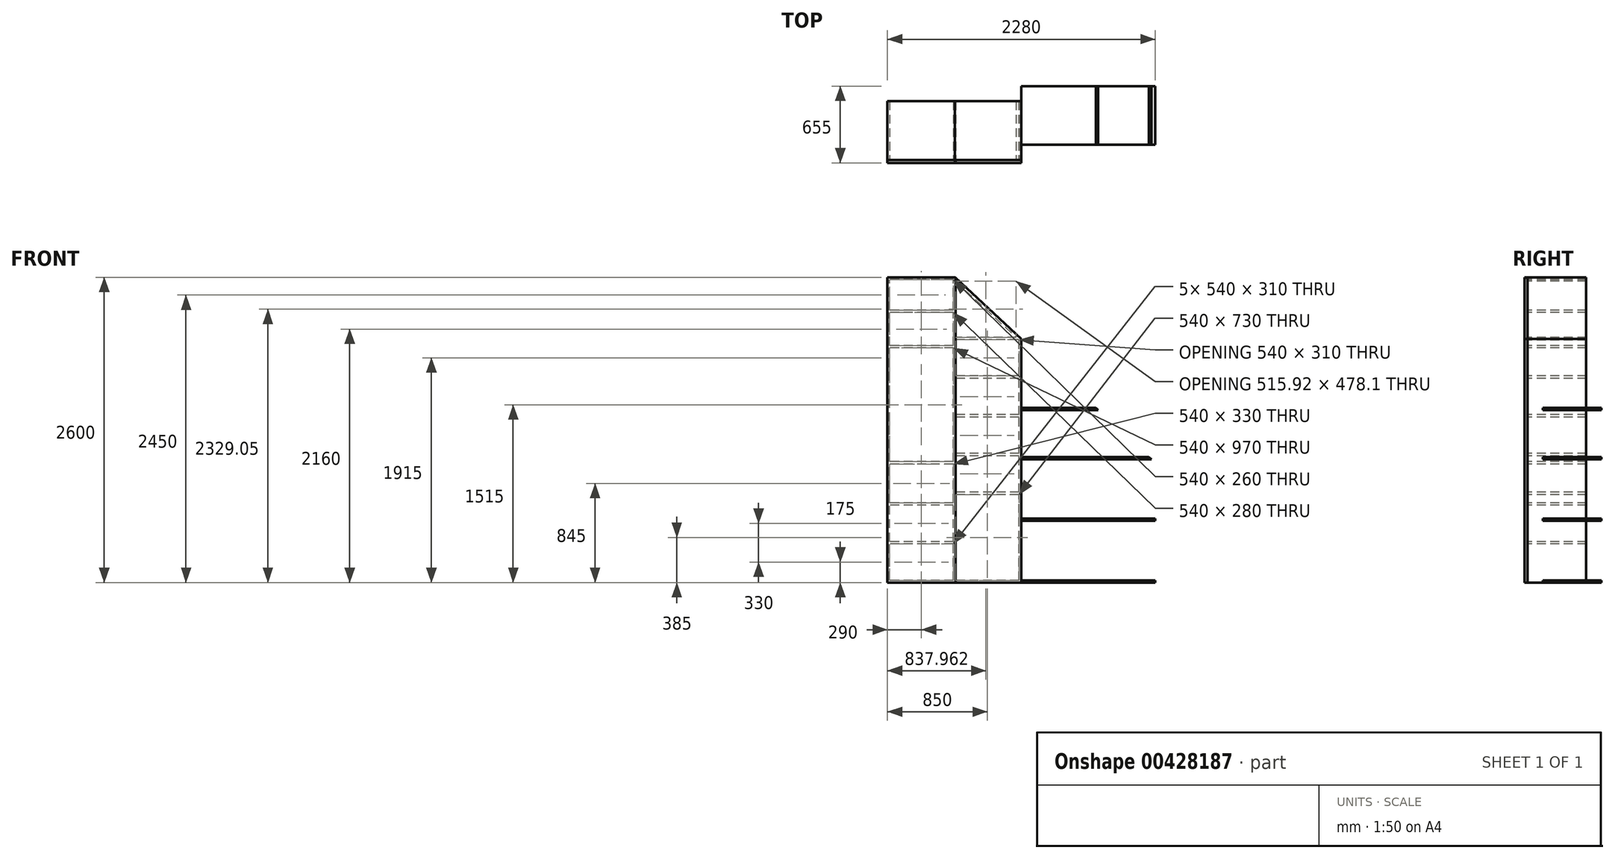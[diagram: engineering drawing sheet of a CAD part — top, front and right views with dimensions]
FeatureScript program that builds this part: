
annotation { "Feature Type Name" : "Feature", "Feature Type Description" : "" }
export const myFeature = defineFeature(function(context is Context, id is Id, definition is map)
    precondition{}
    {
        {
            var Q0;
            Q0=qCreatedBy(makeId("Front.planeOp"),FACE);
            var sketch = newSketch(context, id + "F0", { "sketchPlane" : qUnion([Q0])});
            skLineSegment(sketch, "E0.bottom", {"start": v(1140, -1300) * mm, "end": v(-1140, -1300) * mm});
            skLineSegment(sketch, "E0.top", {"start": v(-565, 1300) * mm, "end": v(-1140, 1300) * mm});
            skLineSegment(sketch, "E0.left", {"start": v(1140, -1300) * mm, "end": v(1140, -280) * mm});
            skLineSegment(sketch, "E0.right", {"start": v(-1140, -1300) * mm, "end": v(-1140, 1300) * mm});
            skPoint(sketch, "E0.middle", {"position": v(0, 0) * mm});
            skLineSegment(sketch, "E1", {"start": v(-565, 1300) * mm, "end": v(1140, -280) * mm});
            skLineSegment(sketch, "E2.0", {"start": v(-20, -1280) * mm, "end": v(-20, -550) * mm});
            skLineSegment(sketch, "E3.0", {"start": v(-580, -1280) * mm, "end": v(-580, -970) * mm});
            skLineSegment(sketch, "E4.0", {"start": v(-20, -1050) * mm, "end": v(-560, -1050) * mm});
            skLineSegment(sketch, "E5.0", {"start": v(-20, -800) * mm, "end": v(-560, -800) * mm});
            skLineSegment(sketch, "E6.0", {"start": v(-20, -550) * mm, "end": v(-560, -550) * mm});
            skLineSegment(sketch, "E7.0", {"start": v(-580, -325) * mm, "end": v(-1120, -325) * mm});
            skLineSegment(sketch, "E8.trimOffspring", {"start": v(-580, 700) * mm, "end": v(-1120, 700) * mm});
            skLineSegment(sketch, "E9.0", {"start": v(-580, 1000) * mm, "end": v(-1120, 1000) * mm});
            skLineSegment(sketch, "E10.0", {"start": v(-580, -640) * mm, "end": v(-1120, -640) * mm});
            skLineSegment(sketch, "E11.trimOffspring", {"start": v(-580, -970) * mm, "end": v(-1120, -970) * mm});
            skLineSegment(sketch, "E12.0", {"start": v(-580, 670) * mm, "end": v(-1120, 670) * mm});
            skLineSegment(sketch, "E13.0", {"start": v(-580, 650) * mm, "end": v(-1120, 650) * mm});
            skLineSegment(sketch, "E14.0", {"start": v(-580, -270) * mm, "end": v(-1120, -270) * mm});
            skLineSegment(sketch, "E15.0", {"start": v(-580, -345) * mm, "end": v(-1120, -345) * mm});
            skLineSegment(sketch, "E16.0", {"start": v(1140, -775) * mm, "end": v(0, -775) * mm});
            skLineSegment(sketch, "E17", {"start": v(1140, -280) * mm, "end": v(0, -280) * mm, "construction": true});
            skLineSegment(sketch, "E18.0", {"start": v(1107.63, -250) * mm, "end": v(-20, -250) * mm});
            skLineSegment(sketch, "E19.0", {"start": v(654.4, 170) * mm, "end": v(0, 170) * mm});
            skLineSegment(sketch, "E20.0", {"start": v(-1120, -1280) * mm, "end": v(-1120, -970) * mm});
            skLineSegment(sketch, "E21.0", {"start": v(-560, -1300) * mm, "end": v(-560, 1268.1) * mm});
            skLineSegment(sketch, "E22.0", {"start": v(0, -1300) * mm, "end": v(0, 776.42) * mm});
            skLineSegment(sketch, "E23.0", {"start": v(-580, 1280) * mm, "end": v(-1120, 1280) * mm});
            skLineSegment(sketch, "E24.0", {"start": v(-560, 1268.1) * mm, "end": v(-44.08, 790) * mm});
            skLineSegment(sketch, "E25.0", {"start": v(1140, -755) * mm, "end": v(0, -755) * mm});
            skLineSegment(sketch, "E26.0", {"start": v(-580, 1020) * mm, "end": v(-1120, 1020) * mm});
            skLineSegment(sketch, "E27.0", {"start": v(-580, 720) * mm, "end": v(-1120, 720) * mm});
            skLineSegment(sketch, "E28.0", {"start": v(-580, -290) * mm, "end": v(-1120, -290) * mm});
            skLineSegment(sketch, "E29.0", {"start": v(-580, -620) * mm, "end": v(-1120, -620) * mm});
            skLineSegment(sketch, "E30.0", {"start": v(-580, -950) * mm, "end": v(-1120, -950) * mm});
            skLineSegment(sketch, "E31.0", {"start": v(1140, -1280) * mm, "end": v(0, -1280) * mm});
            skLineSegment(sketch, "E32.trimOffspring", {"start": v(1086.04, -230) * mm, "end": v(0, -230) * mm});
            skLineSegment(sketch, "E33.trimOffspring", {"start": v(632.82, 190) * mm, "end": v(0, 190) * mm});
            skLineSegment(sketch, "E34.trimOffspring", {"start": v(-1120, 1020) * mm, "end": v(-1120, 1280) * mm});
            skLineSegment(sketch, "E35.trimOffspring", {"start": v(-1120, 720) * mm, "end": v(-1120, 1000) * mm});
            skLineSegment(sketch, "E36.trimOffspring", {"start": v(-580, 720) * mm, "end": v(-580, 1000) * mm});
            skLineSegment(sketch, "E37.trimOffspring", {"start": v(-580, 1020) * mm, "end": v(-580, 1280) * mm});
            skLineSegment(sketch, "E38.trimOffspring", {"start": v(-1120, -270) * mm, "end": v(-1120, 700) * mm});
            skLineSegment(sketch, "E39.trimOffspring", {"start": v(-580, -270) * mm, "end": v(-580, 700) * mm});
            skLineSegment(sketch, "E40.trimOffspring", {"start": v(-20, 375) * mm, "end": v(-20, 440) * mm});
            skLineSegment(sketch, "E41.trimOffspring", {"start": v(-20, 720) * mm, "end": v(-20, 767.69) * mm});
            skPoint(sketch, "E42.orphan", {"position": v(-20, -280) * mm});
            skLineSegment(sketch, "E43.trimOffspring", {"start": v(-20, -285) * mm, "end": v(-20, -220) * mm});
            skPoint(sketch, "E44.orphan", {"position": v(-580, -550) * mm});
            skPoint(sketch, "E45.orphan", {"position": v(-580, -800) * mm});
            skLineSegment(sketch, "E46.trimOffspring", {"start": v(-580, -950) * mm, "end": v(-580, -640) * mm});
            skLineSegment(sketch, "E47.trimOffspring", {"start": v(-580, -620) * mm, "end": v(-580, -290) * mm});
            skLineSegment(sketch, "E48.trimOffspring", {"start": v(-580, -1280) * mm, "end": v(-1120, -1280) * mm});
            skPoint(sketch, "E49.orphan", {"position": v(-1140, -970) * mm});
            skLineSegment(sketch, "E50.trimOffspring", {"start": v(-1120, -950) * mm, "end": v(-1120, -640) * mm});
            skPoint(sketch, "E51.orphan", {"position": v(-1140, -640) * mm});
            skLineSegment(sketch, "E52.trimOffspring", {"start": v(-1120, -620) * mm, "end": v(-1120, -290) * mm});
            skLineSegment(sketch, "E53.trimOffspring", {"start": v(-20, -1280) * mm, "end": v(-560, -1280) * mm});
            skLineSegment(sketch, "E54", {"start": v(-560, 1268.1) * mm, "end": v(-560, 1295.37) * mm});
            skLineSegment(sketch, "E55.0", {"start": v(-20, -220) * mm, "end": v(-560, -220) * mm});
            skLineSegment(sketch, "E56.0", {"start": v(-20, 110) * mm, "end": v(-560, 110) * mm});
            skLineSegment(sketch, "E57.0", {"start": v(-20, 440) * mm, "end": v(-560, 440) * mm});
            skLineSegment(sketch, "E58.0", {"start": v(-20, 770) * mm, "end": v(-560, 770) * mm});
            skLineSegment(sketch, "E59.0", {"start": v(-44.08, 790) * mm, "end": v(-560, 790) * mm});
            skLineSegment(sketch, "E60.0", {"start": v(-20, 460) * mm, "end": v(-560, 460) * mm});
            skLineSegment(sketch, "E61.0", {"start": v(-20, 130) * mm, "end": v(-560, 130) * mm});
            skLineSegment(sketch, "E62.0", {"start": v(-20, -200) * mm, "end": v(-560, -200) * mm});
            skLineSegment(sketch, "E63.0", {"start": v(-20, -530) * mm, "end": v(-560, -530) * mm});
            skLineSegment(sketch, "E64.trimOffspring", {"start": v(-22.5, 770) * mm, "end": v(-20, 767.69) * mm});
            skLineSegment(sketch, "E65.trimOffspring", {"start": v(-20, 460) * mm, "end": v(-20, 700) * mm});
            skLineSegment(sketch, "E66.trimOffspring", {"start": v(-20, 130) * mm, "end": v(-20, 355) * mm});
            skLineSegment(sketch, "E67.trimOffspring", {"start": v(-20, -200) * mm, "end": v(-20, 110) * mm});
            skLineSegment(sketch, "E68.trimOffspring", {"start": v(-20, -530) * mm, "end": v(-20, -305) * mm});
            skLineSegment(sketch, "E69", {"start": v(-20, 720) * mm, "end": v(-20, 700) * mm});
            skLineSegment(sketch, "E70", {"start": v(-20, 375) * mm, "end": v(-20, 355) * mm});
            skLineSegment(sketch, "E71", {"start": v(-20, 130) * mm, "end": v(-20, 110) * mm});
            skLineSegment(sketch, "E72", {"start": v(-20, -285) * mm, "end": v(-20, -305) * mm});
            skSolve(sketch);
        }
        {
            var Q0;
            {var subQ21=sQuery(id+"F0.wireOp",EDGE,"E0.top");Q0=makeQuery(id+"F0.imprint","IMPRINT",FACE,{"disambiguationData":[TD([[makeQuery(id+"F0.imprint","IMPRINT",EDGE,{"derivedFrom":subQ21}),1.0]])]});}
            var Q1;
            {var subQ0=sQuery(id+"F0.wireOp",EDGE,"075f6fa9-2338-4907-bc7f-4152ca9d7cae.0");Q1=makeQuery(id+"F0.imprint","IMPRINT",FACE,{"disambiguationData":[TD([[makeQuery(id+"F0.imprint","IMPRINT",EDGE,{"derivedFrom":subQ0}),-1.0]])]});}
            var Q2;
            {var subQ1=sQuery(id+"F0.wireOp",EDGE,"c482d40b-7409-438c-9fb2-e3521484e001.0");Q2=makeQuery(id+"F0.imprint","IMPRINT",FACE,{"disambiguationData":[TD([[makeQuery(id+"F0.imprint","IMPRINT",EDGE,{"derivedFrom":subQ1}),-1.0]])]});}
            var Q3;
            {var subQ6=sQuery(id+"F0.wireOp",EDGE,"nY6rth7n-ROY5-i2ze-aggr-co93LDrI6tG6");Q3=makeQuery(id+"F0.imprint","IMPRINT",FACE,{"disambiguationData":[TD([[makeQuery(id+"F0.imprint","IMPRINT",EDGE,{"derivedFrom":subQ6}),1.0]])]});}
            var Q4;
            Q4=makeQuery(id+"F0.imprint","IMPRINT",FACE,{"disambiguationData":[TD([[makeQuery(id+"F0.imprint","IMPRINT",EDGE,{"derivedFrom":sQuery(id+"F0.wireOp",EDGE,"E24.0")}),1.0]])]});
            var Q5;
            {var subQ0=sQuery(id+"F0.wireOp",EDGE,"E56.0");Q5=makeQuery(id+"F0.imprint","IMPRINT",FACE,{"disambiguationData":[TD([[makeQuery(id+"F0.imprint","IMPRINT",EDGE,{"derivedFrom":subQ0}),-1.0]])]});}
            var Q6;
            {var subQ4=sQuery(id+"F0.wireOp",EDGE,"E6.0");Q6=makeQuery(id+"F0.imprint","IMPRINT",FACE,{"disambiguationData":[TD([[makeQuery(id+"F0.imprint","IMPRINT",EDGE,{"derivedFrom":subQ4}),-1.0]])]});}
            extrude(context, id + "F1", {"entities" : qUnion([Q0, Q1, Q2, Q3, Q4, Q5, Q6]), "oppositeDirection" : true, "depth" : 500 * mm});
        }
        {
            var Q0;
            Q0=makeQuery(id+"F0.imprint","IMPRINT",FACE,{"disambiguationData":[TD([[makeQuery(id+"F0.imprint","IMPRINT",EDGE,{"derivedFrom":sQuery(id+"F0.wireOp",EDGE,"E23.0")}),1.0]])]});
            var Q1;
            Q1=makeQuery(id+"F0.imprint","IMPRINT",FACE,{"disambiguationData":[TD([[makeQuery(id+"F0.imprint","IMPRINT",EDGE,{"derivedFrom":sQuery(id+"F0.wireOp",EDGE,"E9.0")}),1.0]])]});
            var Q2;
            {var subQ0=sQuery(id+"F0.wireOp",EDGE,"E13.0");Q2=makeQuery(id+"F0.imprint","IMPRINT",FACE,{"disambiguationData":[TD([[makeQuery(id+"F0.imprint","IMPRINT",EDGE,{"derivedFrom":subQ0}),1.0]])]});}
            var Q3;
            {var subQ0=sQuery(id+"F0.wireOp",EDGE,"E12.0");Q3=makeQuery(id+"F0.imprint","IMPRINT",FACE,{"disambiguationData":[TD([[makeQuery(id+"F0.imprint","IMPRINT",EDGE,{"derivedFrom":subQ0}),1.0]])]});}
            var Q4;
            {var subQ0=sQuery(id+"F0.wireOp",EDGE,"E8.trimOffspring");Q4=makeQuery(id+"F0.imprint","IMPRINT",FACE,{"disambiguationData":[TD([[makeQuery(id+"F0.imprint","IMPRINT",EDGE,{"derivedFrom":subQ0}),1.0]])]});}
            var Q5;
            {var subQ0=sQuery(id+"F0.wireOp",EDGE,"E7.0");Q5=makeQuery(id+"F0.imprint","IMPRINT",FACE,{"disambiguationData":[TD([[makeQuery(id+"F0.imprint","IMPRINT",EDGE,{"derivedFrom":subQ0}),-1.0]])]});}
            var Q6;
            {var subQ0=sQuery(id+"F0.wireOp",EDGE,"E7.0");Q6=makeQuery(id+"F0.imprint","IMPRINT",FACE,{"disambiguationData":[TD([[makeQuery(id+"F0.imprint","IMPRINT",EDGE,{"derivedFrom":subQ0}),1.0]])]});}
            var Q7;
            {var subQ0=sQuery(id+"F0.wireOp",EDGE,"E15.0");Q7=makeQuery(id+"F0.imprint","IMPRINT",FACE,{"disambiguationData":[TD([[makeQuery(id+"F0.imprint","IMPRINT",EDGE,{"derivedFrom":subQ0}),1.0]])]});}
            var Q8;
            Q8=makeQuery(id+"F0.imprint","IMPRINT",FACE,{"disambiguationData":[TD([[makeQuery(id+"F0.imprint","IMPRINT",EDGE,{"derivedFrom":sQuery(id+"F0.wireOp",EDGE,"E10.0")}),1.0]])]});
            var Q9;
            Q9=makeQuery(id+"F0.imprint","IMPRINT",FACE,{"disambiguationData":[TD([[makeQuery(id+"F0.imprint","IMPRINT",EDGE,{"derivedFrom":sQuery(id+"F0.wireOp",EDGE,"E3.0")}),1.0]])]});
            var Q10;
            {var subQ29=sQuery(id+"F0.wireOp",EDGE,"E0.top");Q10=makeQuery(id+"F0.imprint","IMPRINT",FACE,{"disambiguationData":[TD([[makeQuery(id+"F0.imprint","IMPRINT",EDGE,{"derivedFrom":subQ29}),1.0]])]});}
            extrude(context, id + "F2", {"entities" : qUnion([Q0, Q1, Q2, Q3, Q4, Q5, Q6, Q7, Q8, Q9, Q10]), "depth" : 25 * mm});
        }
        {
            var Q0;
            {var subQ0=sQuery(id+"F0.wireOp",EDGE,"E24.0");Q0=makeQuery(id+"F0.imprint","IMPRINT",FACE,{"disambiguationData":[TD([[makeQuery(id+"F0.imprint","IMPRINT",EDGE,{"derivedFrom":subQ0}),-1.0]])]});}
            var Q1;
            {var subQ6=sQuery(id+"F0.wireOp",EDGE,"nY6rth7n-ROY5-i2ze-aggr-co93LDrI6tG6");Q1=makeQuery(id+"F0.imprint","IMPRINT",FACE,{"disambiguationData":[TD([[makeQuery(id+"F0.imprint","IMPRINT",EDGE,{"derivedFrom":subQ6}),1.0]])]});}
            var Q2;
            {var subQ0=sQuery(id+"F0.wireOp",EDGE,"nY6rth7n-ROY5-i2ze-aggr-co93LDrI6tG6");Q2=makeQuery(id+"F0.imprint","IMPRINT",FACE,{"disambiguationData":[TD([[makeQuery(id+"F0.imprint","IMPRINT",EDGE,{"derivedFrom":subQ0}),-1.0]])]});}
            var Q3;
            {var subQ0=sQuery(id+"F0.wireOp",EDGE,"7d27a3c1-d96e-461f-ac1f-f439f4170e25.0");Q3=makeQuery(id+"F0.imprint","IMPRINT",FACE,{"disambiguationData":[TD([[makeQuery(id+"F0.imprint","IMPRINT",EDGE,{"derivedFrom":subQ0}),1.0]])]});}
            var Q4;
            {var subQ4=sQuery(id+"F0.wireOp",EDGE,"075f6fa9-2338-4907-bc7f-4152ca9d7cae.0");Q4=makeQuery(id+"F0.imprint","IMPRINT",FACE,{"disambiguationData":[TD([[makeQuery(id+"F0.imprint","IMPRINT",EDGE,{"derivedFrom":subQ4}),1.0]])]});}
            var Q5;
            {var subQ0=sQuery(id+"F0.wireOp",EDGE,"075f6fa9-2338-4907-bc7f-4152ca9d7cae.0");Q5=makeQuery(id+"F0.imprint","IMPRINT",FACE,{"disambiguationData":[TD([[makeQuery(id+"F0.imprint","IMPRINT",EDGE,{"derivedFrom":subQ0}),-1.0]])]});}
            var Q6;
            {var subQ2=sQuery(id+"F0.wireOp",EDGE,"E6.0");Q6=makeQuery(id+"F0.imprint","IMPRINT",FACE,{"disambiguationData":[TD([[makeQuery(id+"F0.imprint","IMPRINT",EDGE,{"derivedFrom":subQ2}),-1.0]])]});}
            var Q7;
            {var subQ5=sQuery(id+"F0.wireOp",EDGE,"c482d40b-7409-438c-9fb2-e3521484e001.0");Q7=makeQuery(id+"F0.imprint","IMPRINT",FACE,{"disambiguationData":[TD([[makeQuery(id+"F0.imprint","IMPRINT",EDGE,{"derivedFrom":subQ5}),-1.0]])]});}
            var Q8;
            {var subQ0=sQuery(id+"F0.wireOp",EDGE,"E5.0");Q8=makeQuery(id+"F0.imprint","IMPRINT",FACE,{"disambiguationData":[TD([[makeQuery(id+"F0.imprint","IMPRINT",EDGE,{"derivedFrom":subQ0}),-1.0]])]});}
            var Q9;
            {var subQ0=sQuery(id+"F0.wireOp",EDGE,"E4.0");Q9=makeQuery(id+"F0.imprint","IMPRINT",FACE,{"disambiguationData":[TD([[makeQuery(id+"F0.imprint","IMPRINT",EDGE,{"derivedFrom":subQ0}),-1.0]])]});}
            var Q10;
            {var subQ2=sQuery(id+"F0.wireOp",EDGE,"E4.0");Q10=makeQuery(id+"F0.imprint","IMPRINT",FACE,{"disambiguationData":[TD([[makeQuery(id+"F0.imprint","IMPRINT",EDGE,{"derivedFrom":subQ2}),1.0]])]});}
            var Q11;
            {var subQ0=sQuery(id+"F0.wireOp",EDGE,"E55.0");Q11=makeQuery(id+"F0.imprint","IMPRINT",FACE,{"disambiguationData":[TD([[makeQuery(id+"F0.imprint","IMPRINT",EDGE,{"derivedFrom":subQ0}),1.0]])]});}
            var Q12;
            Q12=makeQuery(id+"F0.imprint","IMPRINT",FACE,{"disambiguationData":[TD([[makeQuery(id+"F0.imprint","IMPRINT",EDGE,{"derivedFrom":sQuery(id+"F0.wireOp",EDGE,"E24.0")}),1.0]])]});
            var Q13;
            {var subQ0=sQuery(id+"F0.wireOp",EDGE,"E56.0");Q13=makeQuery(id+"F0.imprint","IMPRINT",FACE,{"disambiguationData":[TD([[makeQuery(id+"F0.imprint","IMPRINT",EDGE,{"derivedFrom":subQ0}),1.0]])]});}
            var Q14;
            {var subQ0=sQuery(id+"F0.wireOp",EDGE,"E56.0");Q14=makeQuery(id+"F0.imprint","IMPRINT",FACE,{"disambiguationData":[TD([[makeQuery(id+"F0.imprint","IMPRINT",EDGE,{"derivedFrom":subQ0}),-1.0]])]});}
            var Q15;
            Q15=makeQuery(id+"F0.imprint","IMPRINT",FACE,{"disambiguationData":[TD([[makeQuery(id+"F0.imprint","IMPRINT",EDGE,{"derivedFrom":sQuery(id+"F0.wireOp",EDGE,"E40.trimOffspring")}),1.0]])]});
            var Q16;
            Q16=makeQuery(id+"F0.imprint","IMPRINT",FACE,{"disambiguationData":[TD([[makeQuery(id+"F0.imprint","IMPRINT",EDGE,{"derivedFrom":sQuery(id+"F0.wireOp",EDGE,"E41.trimOffspring")}),1.0]])]});
            extrude(context, id + "F3", {"entities" : qUnion([Q0, Q1, Q2, Q3, Q4, Q5, Q6, Q7, Q8, Q9, Q10, Q11, Q12, Q13, Q14, Q15, Q16]), "depth" : 25 * mm});
        }
        {
            var Q0;
            {var subQ0=sQuery(id+"F0.wireOp",EDGE,"E19.0");Q0=makeQuery(id+"F0.imprint","IMPRINT",FACE,{"disambiguationData":[TD([[makeQuery(id+"F0.imprint","IMPRINT",EDGE,{"derivedFrom":subQ0}),-1.0]])]});}
            var Q1;
            {var subQ3=sQuery(id+"F0.wireOp",EDGE,"E32.trimOffspring");Q1=makeQuery(id+"F0.imprint","IMPRINT",FACE,{"disambiguationData":[TD([[makeQuery(id+"F0.imprint","IMPRINT",EDGE,{"derivedFrom":subQ3}),1.0]])]});}
            var Q2;
            {var subQ0=sQuery(id+"F0.wireOp",EDGE,"E16.0");Q2=makeQuery(id+"F0.imprint","IMPRINT",FACE,{"disambiguationData":[TD([[makeQuery(id+"F0.imprint","IMPRINT",EDGE,{"derivedFrom":subQ0}),-1.0]])]});}
            var Q3;
            {var subQ5=sQuery(id+"F0.wireOp",EDGE,"E31.0");Q3=makeQuery(id+"F0.imprint","IMPRINT",FACE,{"disambiguationData":[TD([[makeQuery(id+"F0.imprint","IMPRINT",EDGE,{"derivedFrom":subQ5}),1.0]])]});}
            extrude(context, id + "F4", {"entities" : qUnion([Q0, Q1, Q2, Q3]), "oppositeDirection" : true, "depth" : 630 * mm, "hasSecondDirection" : true, "secondDirectionOppositeDirection" : true, "secondDirectionDepth" : 130 * mm});
        }
    });
